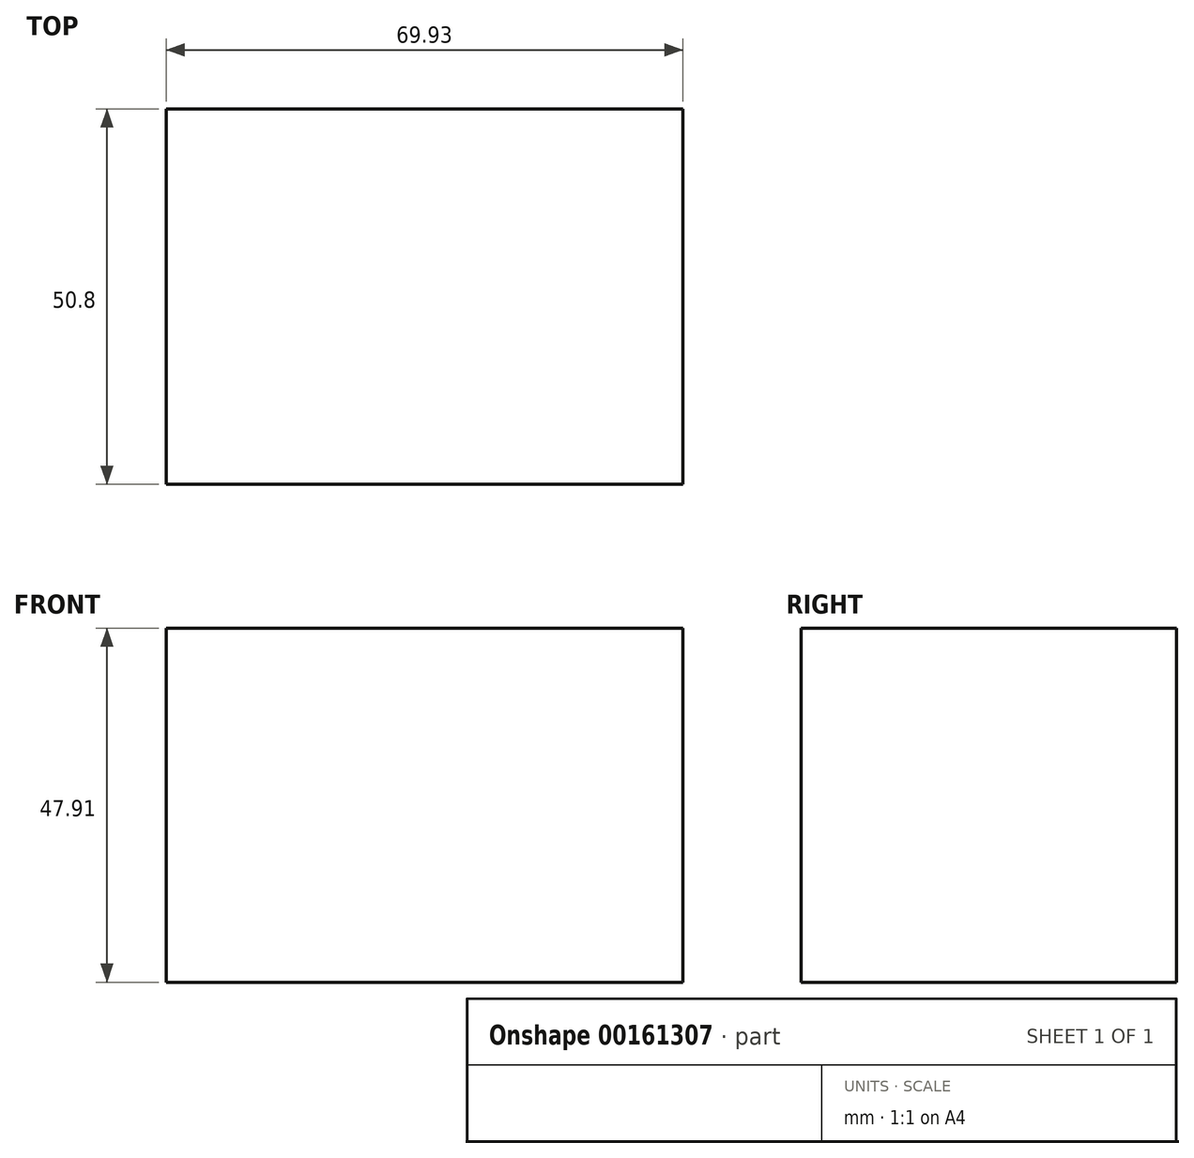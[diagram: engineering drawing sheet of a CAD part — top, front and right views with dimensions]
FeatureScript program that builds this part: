
annotation { "Feature Type Name" : "Feature", "Feature Type Description" : "" }
export const myFeature = defineFeature(function(context is Context, id is Id, definition is map)
    precondition{}
    {
        {
            var Q0;
            Q0=qCreatedBy(makeId("Front.planeOp"),FACE);
            var sketch = newSketch(context, id + "F0", { "sketchPlane" : qUnion([Q0])});
            skLineSegment(sketch, "E0.bottom", {"start": v(0, 0) * mm, "end": v(69.93, 0) * mm});
            skLineSegment(sketch, "E0.top", {"start": v(0, 47.9) * mm, "end": v(69.93, 47.9) * mm});
            skLineSegment(sketch, "E0.left", {"start": v(0, 0) * mm, "end": v(0, 47.9) * mm});
            skLineSegment(sketch, "E0.right", {"start": v(69.93, 0) * mm, "end": v(69.93, 47.9) * mm});
            skSolve(sketch);
        }
        {
            var Q0;
            Q0 = qSketchRegion(id + "F0", true);
            extrude(context, id + "F1", {"entities" : qUnion([Q0]), "depth" : 50.8 * mm});
        }
    });
